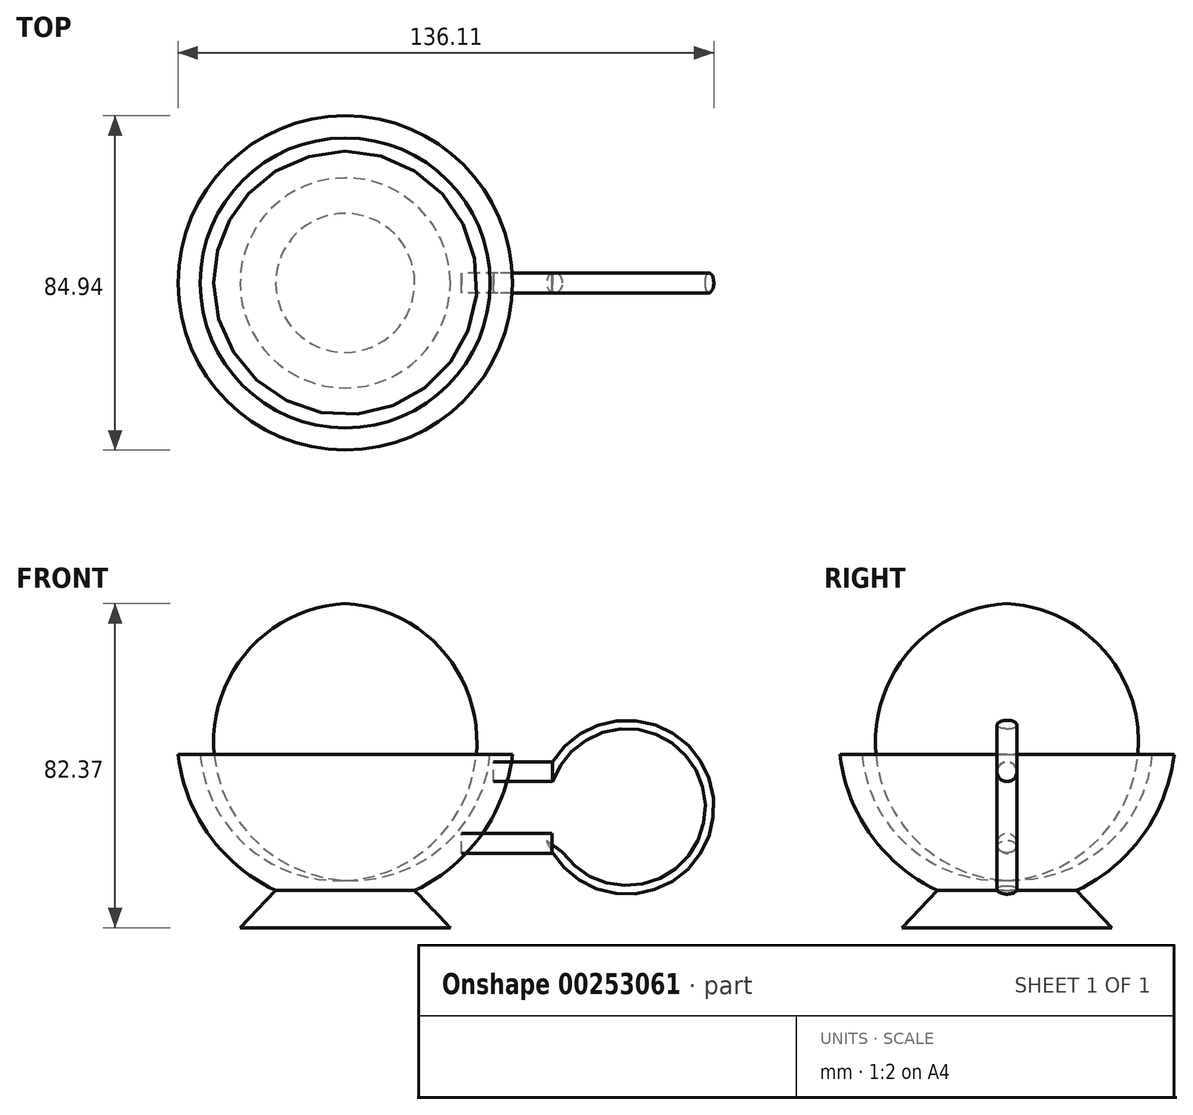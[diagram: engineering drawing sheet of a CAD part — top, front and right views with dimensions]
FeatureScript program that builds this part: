
annotation { "Feature Type Name" : "Feature", "Feature Type Description" : "" }
export const myFeature = defineFeature(function(context is Context, id is Id, definition is map)
    precondition{}
    {
        {
            var Q0;
            Q0=qCreatedBy(makeId("Front.planeOp"),FACE);
            var sketch = newSketch(context, id + "F0", { "sketchPlane" : qUnion([Q0])});
            skArc(sketch, "E0", {"start": v(-36.83, 31.95) * mm, "mid": v(-24.84, 8.57) * mm, "end": v(0, 0) * mm});
            skArc(sketch, "E1", {"start": v(-42.47, 31.95) * mm, "mid": v(-28.46, 4.66) * mm, "end": v(0, -6.77) * mm});
            skLineSegment(sketch, "E2", {"start": v(-42.47, 31.95) * mm, "end": v(-36.83, 31.95) * mm});
            skLineSegment(sketch, "E3", {"start": v(0, -6.77) * mm, "end": v(0, 0) * mm});
            skLineSegment(sketch, "E4", {"start": v(0, 49.61) * mm, "end": v(0, -44.73) * mm, "construction": true});
            skLineSegment(sketch, "E5", {"start": v(-17.64, -2.59) * mm, "end": v(-26.69, -12.03) * mm});
            skLineSegment(sketch, "E6", {"start": v(-26.69, -12.03) * mm, "end": v(0, -12.03) * mm});
            skLineSegment(sketch, "E7", {"start": v(0, -12.03) * mm, "end": v(0, -6.77) * mm});
            skSolve(sketch);
        }
        {
            var Q0;
            Q0 = qSketchRegion(id + "F0", true);
            var Q1;
            Q1=sQuery(id+"F0.wireOp",EDGE,"E4");
            revolve(context, id + "F1", {"entities" : qUnion([Q0]), "axis" : qUnion([Q1]), "revolveType" : RevolveType.FULL});
        }
        {
            var Q0;
            Q0=qCreatedBy(makeId("Front.planeOp"),FACE);
            var sketch = newSketch(context, id + "F2", { "sketchPlane" : qUnion([Q0])});
            skLineSegment(sketch, "E8", {"start": v(0, 27.72) * mm, "end": v(37.7, 27.72) * mm});
            skLineSegment(sketch, "E9", {"start": v(0, 9.05) * mm, "end": v(29.58, 9.05) * mm});
            skSolve(sketch);
        }
        {
            var Q0;
            Q0=qCreatedBy(makeId("Right.planeOp"),FACE);
            var sketch = newSketch(context, id + "F3", { "sketchPlane" : qUnion([Q0])});
            skCircle(sketch, "E10", {"center": v(0, 27.63) * mm, "radius": 2.52 * mm});
            skCircle(sketch, "E11", {"center": v(0, 9.4) * mm, "radius": 2.54 * mm});
            skSolve(sketch);
        }
        {
            var Q0;
            Q0=makeQuery(id+"F3.imprint","IMPRINT",FACE,{"disambiguationData":[TD([[makeQuery(id+"F3.imprint","IMPRINT",EDGE,{"derivedFrom":sQuery(id+"F3.wireOp",EDGE,"E10")}),1.0]])]});
            extrude(context, id + "F4", {"entities" : qUnion([Q0]), "depth" : 15 * mm});
        }
        {
            var Q0;
            Q0=qCreatedBy(makeId("Right.planeOp"),FACE);
            var sketch = newSketch(context, id + "F5", { "sketchPlane" : qUnion([Q0])});
            skCircle(sketch, "E12", {"center": v(0, 27.7) * mm, "radius": 2.52 * mm});
            skCircle(sketch, "E13", {"center": v(0, 9.4) * mm, "radius": 2.52 * mm});
            skSolve(sketch);
        }
        {
            var Q0;
            Q0=makeQuery(id+"F5.imprint","IMPRINT",FACE,{"disambiguationData":[TD([[makeQuery(id+"F5.imprint","IMPRINT",EDGE,{"derivedFrom":sQuery(id+"F5.wireOp",EDGE,"E13")}),1.0]])]});
            extrude(context, id + "F6", {"entities" : qUnion([Q0]), "depth" : 23 * mm});
        }
        {
            var Q0;
            Q0=makeQuery(id+"F4.opExtrude","SWEPT_BODY",BODY,{"disambiguationData":[OSD([sQuery(id+"F3.wireOp",EDGE,"E10")])]});
            var Q1;
            Q1=sQuery(id+"F2.wireOp",EDGE,"E8");
            transform(context, id + "F7", {"entities" : qUnion([Q0]), "transformType" : TransformType.TRANSLATION_ENTITY, "oppositeDirectionEntity" : false, "transformLine" : qUnion([Q1]), "makeCopy" : false});
        }
        {
            var Q0;
            Q0=makeQuery(id+"F6.opExtrude","SWEPT_BODY",BODY,{"disambiguationData":[OSD([sQuery(id+"F5.wireOp",EDGE,"E13")])]});
            var Q1;
            Q1=sQuery(id+"F2.wireOp",EDGE,"E9");
            transform(context, id + "F8", {"entities" : qUnion([Q0]), "transformType" : TransformType.TRANSLATION_ENTITY, "oppositeDirectionEntity" : false, "transformLine" : qUnion([Q1]), "makeCopy" : false});
        }
        {
            var Q0;
            Q0=qCreatedBy(makeId("Front.planeOp"),FACE);
            var sketch = newSketch(context, id + "F9", { "sketchPlane" : qUnion([Q0])});
            skArc(sketch, "E14", {"start": v(52.63, 9.02) * mm, "mid": v(92.74, 18.6) * mm, "end": v(52.63, 28.2) * mm});
            skLineSegment(sketch, "E15", {"start": v(52.63, 26.31) * mm, "end": v(52.63, 6.58) * mm, "construction": true});
            skSolve(sketch);
        }
        {
            var Q0;
            Q0=makeQuery(id+"F4.opExtrude","CAP_FACE",FACE,{"disambiguationData":[OSD([sQuery(id+"F3.wireOp",EDGE,"E10")])],"isStart":false});
            var Q1;
            Q1=sQuery(id+"F9.wireOp",EDGE,"E14");
            sweep(context, id + "F10", {"profiles" : qUnion([Q0]), "path" : qUnion([Q1])});
        }
    });
